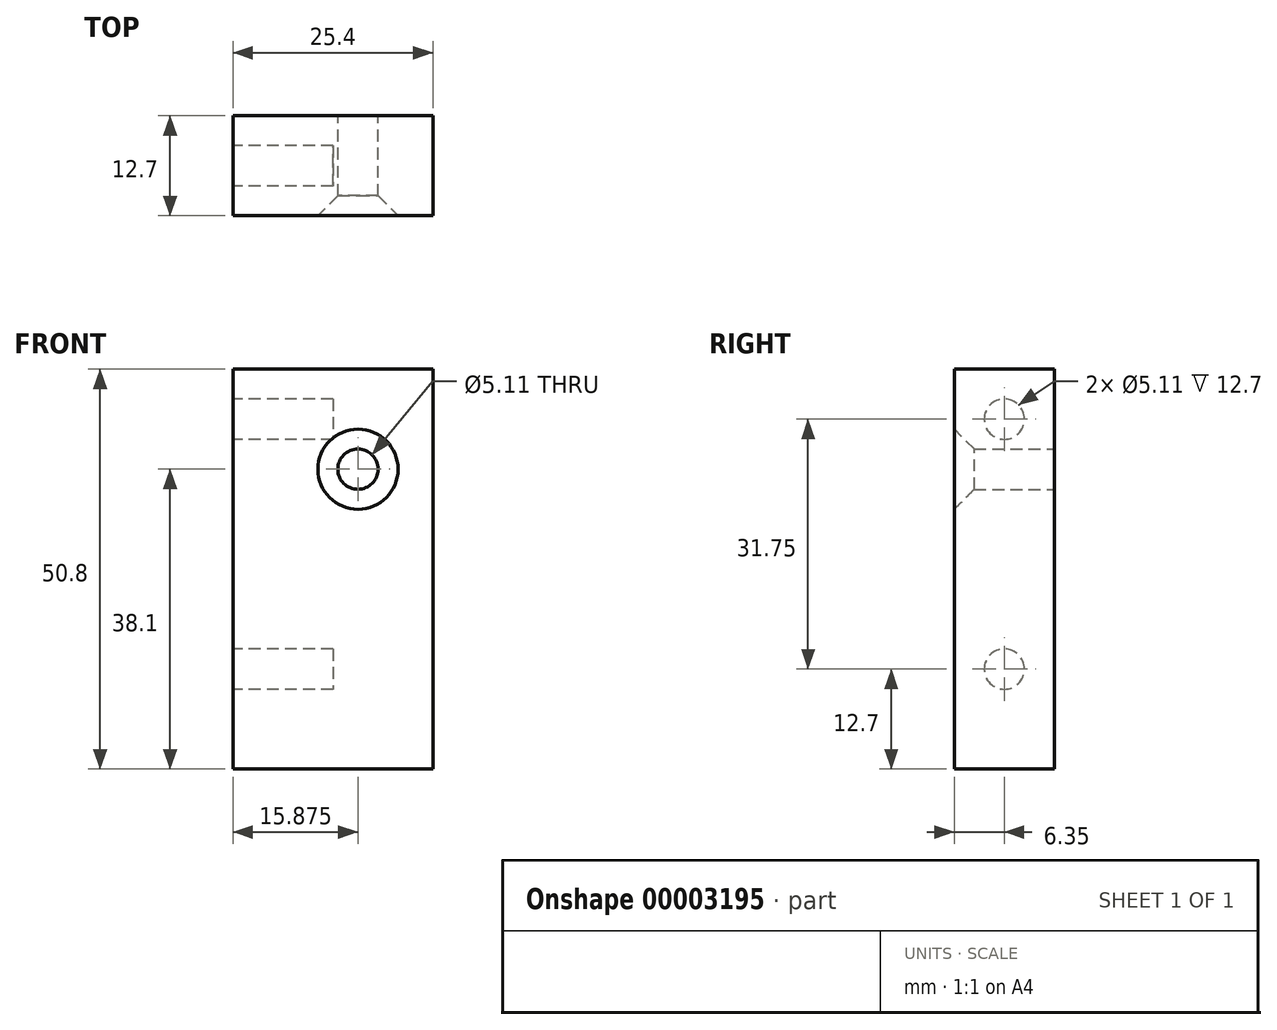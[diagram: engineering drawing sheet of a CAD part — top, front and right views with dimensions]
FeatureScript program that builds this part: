
annotation { "Feature Type Name" : "Feature", "Feature Type Description" : "" }
export const myFeature = defineFeature(function(context is Context, id is Id, definition is map)
    precondition{}
    {
        {
            var Q0;
            Q0=qCreatedBy(makeId("Front.planeOp"),FACE);
            var sketch = newSketch(context, id + "F0", { "sketchPlane" : qUnion([Q0])});
            skLineSegment(sketch, "E0", {"start": v(0, 0) * mm, "end": v(0, -50.8) * mm});
            skLineSegment(sketch, "E1", {"start": v(0, -50.8) * mm, "end": v(25.4, -50.8) * mm});
            skLineSegment(sketch, "E2", {"start": v(25.4, -50.8) * mm, "end": v(25.4, 0) * mm});
            skLineSegment(sketch, "E3", {"start": v(25.4, 0) * mm, "end": v(0, 0) * mm});
            skLineSegment(sketch, "E4", {"start": v(15.88, 0) * mm, "end": v(15.88, -50.8) * mm, "construction": true});
            skLineSegment(sketch, "E5", {"start": v(0, -12.7) * mm, "end": v(25.4, -12.7) * mm, "construction": true});
            skCircle(sketch, "E6", {"center": v(15.88, -12.7) * mm, "radius": 2.55 * mm});
            skSolve(sketch);
        }
        {
            var Q0;
            Q0=makeQuery(id+"F0.imprint","IMPRINT",FACE,{"disambiguationData":[TD([[makeQuery(id+"F0.imprint","IMPRINT",EDGE,{"derivedFrom":sQuery(id+"F0.wireOp",EDGE,"E0")}),1.0]])]});
            extrude(context, id + "F1", {"entities" : qUnion([Q0]), "endBound" : BoundingType.SYMMETRIC, "depth" : 12.7 * mm});
        }
        {
            var Q0;
            Q0=makeQuery(id+"F1.opExtrude","SWEPT_FACE",FACE,{"disambiguationData":[OSD([sQuery(id+"F0.wireOp",EDGE,"E0")])]});
            var sketch = newSketch(context, id + "F2", { "sketchPlane" : qUnion([Q0])});
            skLineSegment(sketch, "E7", {"start": v(0, 0) * mm, "end": v(0, -50.8) * mm, "construction": true});
            skLineSegment(sketch, "E8", {"start": v(-6.35, -6.35) * mm, "end": v(6.35, -6.35) * mm, "construction": true});
            skLineSegment(sketch, "E9", {"start": v(-6.35, -38.1) * mm, "end": v(6.35, -38.1) * mm});
            skCircle(sketch, "E10", {"center": v(0, -6.35) * mm, "radius": 2.55 * mm});
            skCircle(sketch, "E11", {"center": v(0, -38.1) * mm, "radius": 2.55 * mm});
            skSolve(sketch);
        }
        {
            var Q0;
            Q0=makeQuery(id+"F2.imprint","IMPRINT",FACE,{"disambiguationData":[TD([[makeQuery(id+"F2.imprint","IMPRINT",EDGE,{"derivedFrom":sQuery(id+"F2.wireOp",EDGE,"E10")}),1.0]])]});
            var Q1;
            {var subQ0=sQuery(id+"F2.wireOp",EDGE,"E11");var subQ1=sQuery(id+"F2.wireOp",EDGE,"E9");var subQ3=makeQuery(id+"F2.imprint","INTERSECT",VERTEX,{"disambiguationData":[OD(0.0)],"derivedFrom":[subQ1,subQ0]});Q1=makeQuery(id+"F2.imprint","IMPRINT",FACE,{"disambiguationData":[TD([[makeQuery(id+"F2.imprint","IMPRINT",EDGE,{"disambiguationData":[TD([[subQ3,-1.0]])],"derivedFrom":subQ1}),1.0]])]});}
            var Q2;
            {var subQ0=sQuery(id+"F2.wireOp",EDGE,"E11");var subQ1=sQuery(id+"F2.wireOp",EDGE,"E9");var subQ3=makeQuery(id+"F2.imprint","INTERSECT",VERTEX,{"disambiguationData":[OD(0.0)],"derivedFrom":[subQ1,subQ0]});Q2=makeQuery(id+"F2.imprint","IMPRINT",FACE,{"disambiguationData":[TD([[makeQuery(id+"F2.imprint","IMPRINT",EDGE,{"disambiguationData":[TD([[subQ3,-1.0]])],"derivedFrom":subQ1}),-1.0]])]});}
            extrude(context, id + "F3", {"entities" : qUnion([Q0, Q1, Q2]), "operationType" : NewBodyOperationType.REMOVE, "oppositeDirection" : true, "depth" : 12.7 * mm});
        }
        {
            var Q0;
            Q0=makeQuery(id+"F1.opExtrude","CAP_EDGE",EDGE,{"disambiguationData":[OSD([sQuery(id+"F0.wireOp",EDGE,"E6")])],"isStart":false});
            chamfer(context, id + "F4", {"entities" : qUnion([Q0]), "chamferType" : ChamferType.OFFSET_ANGLE, "width" : 2.54 * mm, "oppositeDirection" : false, "angle" : 45 * degree, "tangentPropagation" : true});
        }
    });
